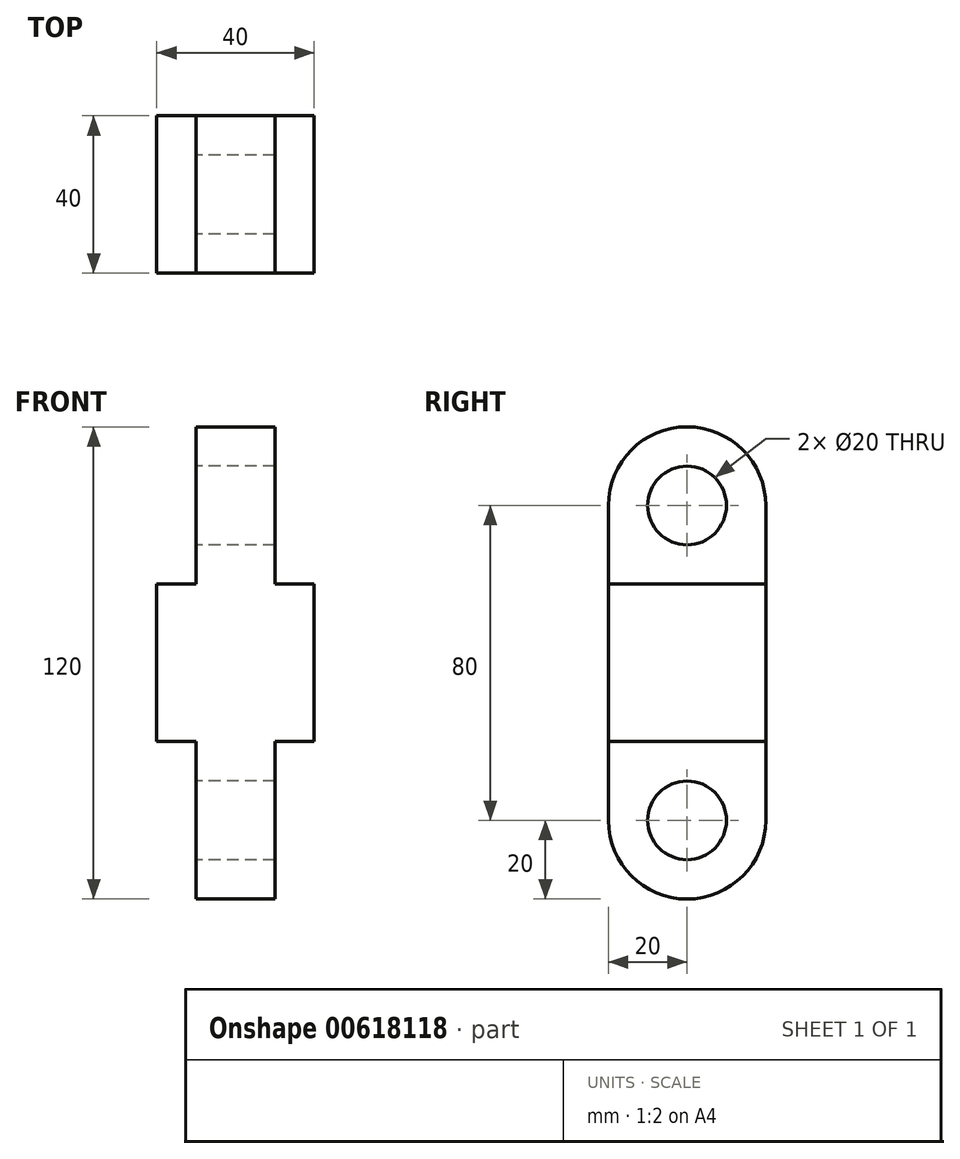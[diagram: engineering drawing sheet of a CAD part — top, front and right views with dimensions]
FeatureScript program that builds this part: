
annotation { "Feature Type Name" : "Feature", "Feature Type Description" : "" }
export const myFeature = defineFeature(function(context is Context, id is Id, definition is map)
    precondition{}
    {
        {
            var Q0;
            Q0=qCreatedBy(makeId("Front.planeOp"),FACE);
            var sketch = newSketch(context, id + "F0", { "sketchPlane" : qUnion([Q0])});
            skLineSegment(sketch, "E0", {"start": v(23.91, 0) * mm, "end": v(23.91, 40) * mm});
            skLineSegment(sketch, "E1", {"start": v(23.91, 40) * mm, "end": v(33.91, 40) * mm});
            skLineSegment(sketch, "E2", {"start": v(33.91, 40) * mm, "end": v(33.91, 80) * mm});
            skLineSegment(sketch, "E3", {"start": v(33.91, 80) * mm, "end": v(23.91, 80) * mm});
            skLineSegment(sketch, "E4", {"start": v(23.91, 80) * mm, "end": v(23.91, 120) * mm});
            skLineSegment(sketch, "E5", {"start": v(3.91, 120) * mm, "end": v(3.91, 80) * mm});
            skLineSegment(sketch, "E6", {"start": v(3.91, 80) * mm, "end": v(-6.09, 80) * mm});
            skLineSegment(sketch, "E7", {"start": v(-6.09, 80) * mm, "end": v(-6.09, 40) * mm});
            skLineSegment(sketch, "E8", {"start": v(-6.09, 40) * mm, "end": v(3.91, 40) * mm});
            skLineSegment(sketch, "E9", {"start": v(3.91, 40) * mm, "end": v(3.91, 0) * mm});
            skPoint(sketch, "E10.center.orphan", {"position": v(13.91, 120) * mm});
            skPoint(sketch, "E11.center.orphan", {"position": v(13.91, 0) * mm});
            skLineSegment(sketch, "E12", {"start": v(3.91, 120) * mm, "end": v(23.91, 120) * mm});
            skLineSegment(sketch, "E13", {"start": v(3.91, 0) * mm, "end": v(23.91, 0) * mm});
            skSolve(sketch);
        }
        {
            var Q0;
            Q0 = qSketchRegion(id + "F0", true);
            extrude(context, id + "F1", {"entities" : qUnion([Q0]), "depth" : 40 * mm, "offsetDistance" : 25 * mm});
        }
        {
            var Q0;
            Q0=makeQuery(id+"F1.opExtrude","CAP_EDGE",EDGE,{"disambiguationData":[OSD([sQuery(id+"F0.wireOp",EDGE,"E12")])],"isStart":true});
            var Q1;
            Q1=makeQuery(id+"F1.opExtrude","CAP_EDGE",EDGE,{"disambiguationData":[OSD([sQuery(id+"F0.wireOp",EDGE,"E12")])],"isStart":false});
            fillet(context, id + "F2", {"entities" : qUnion([Q0, Q1]), "radius" : 20 * mm, "tangentPropagation" : true, "allowEdgeOverflow" : false});
        }
        {
            var Q0;
            Q0=makeQuery(id+"F1.opExtrude","CAP_EDGE",EDGE,{"disambiguationData":[OSD([sQuery(id+"F0.wireOp",EDGE,"E13")])],"isStart":false});
            var Q1;
            Q1=makeQuery(id+"F1.opExtrude","CAP_EDGE",EDGE,{"disambiguationData":[OSD([sQuery(id+"F0.wireOp",EDGE,"E13")])],"isStart":true});
            fillet(context, id + "F3", {"entities" : qUnion([Q0, Q1]), "radius" : 20 * mm, "tangentPropagation" : true, "allowEdgeOverflow" : false});
        }
        {
            var Q0;
            Q0=makeQuery(id+"F1.opExtrude","SWEPT_FACE",FACE,{"disambiguationData":[OSD([sQuery(id+"F0.wireOp",EDGE,"E5")])]});
            var sketch = newSketch(context, id + "F4", { "sketchPlane" : qUnion([Q0])});
            skCircle(sketch, "E14", {"center": v(20, 100) * mm, "radius": 10 * mm});
            skSolve(sketch);
        }
        {
            var Q0;
            Q0 = qSketchRegion(id + "F4", true);
            extrude(context, id + "F5", {"entities" : qUnion([Q0]), "operationType" : NewBodyOperationType.REMOVE, "endBound" : BoundingType.UP_TO_NEXT, "oppositeDirection" : true, "depth" : 25 * mm, "offsetDistance" : 25 * mm});
        }
        {
            var Q0;
            Q0=makeQuery(id+"F1.opExtrude","SWEPT_FACE",FACE,{"disambiguationData":[OSD([sQuery(id+"F0.wireOp",EDGE,"E9")])]});
            var sketch = newSketch(context, id + "F6", { "sketchPlane" : qUnion([Q0])});
            skCircle(sketch, "E15", {"center": v(20, 20) * mm, "radius": 10 * mm});
            skSolve(sketch);
        }
        {
            var Q0;
            Q0 = qSketchRegion(id + "F6", true);
            extrude(context, id + "F7", {"entities" : qUnion([Q0]), "operationType" : NewBodyOperationType.REMOVE, "endBound" : BoundingType.UP_TO_NEXT, "oppositeDirection" : true, "depth" : 25 * mm, "offsetDistance" : 25 * mm});
        }
    });
